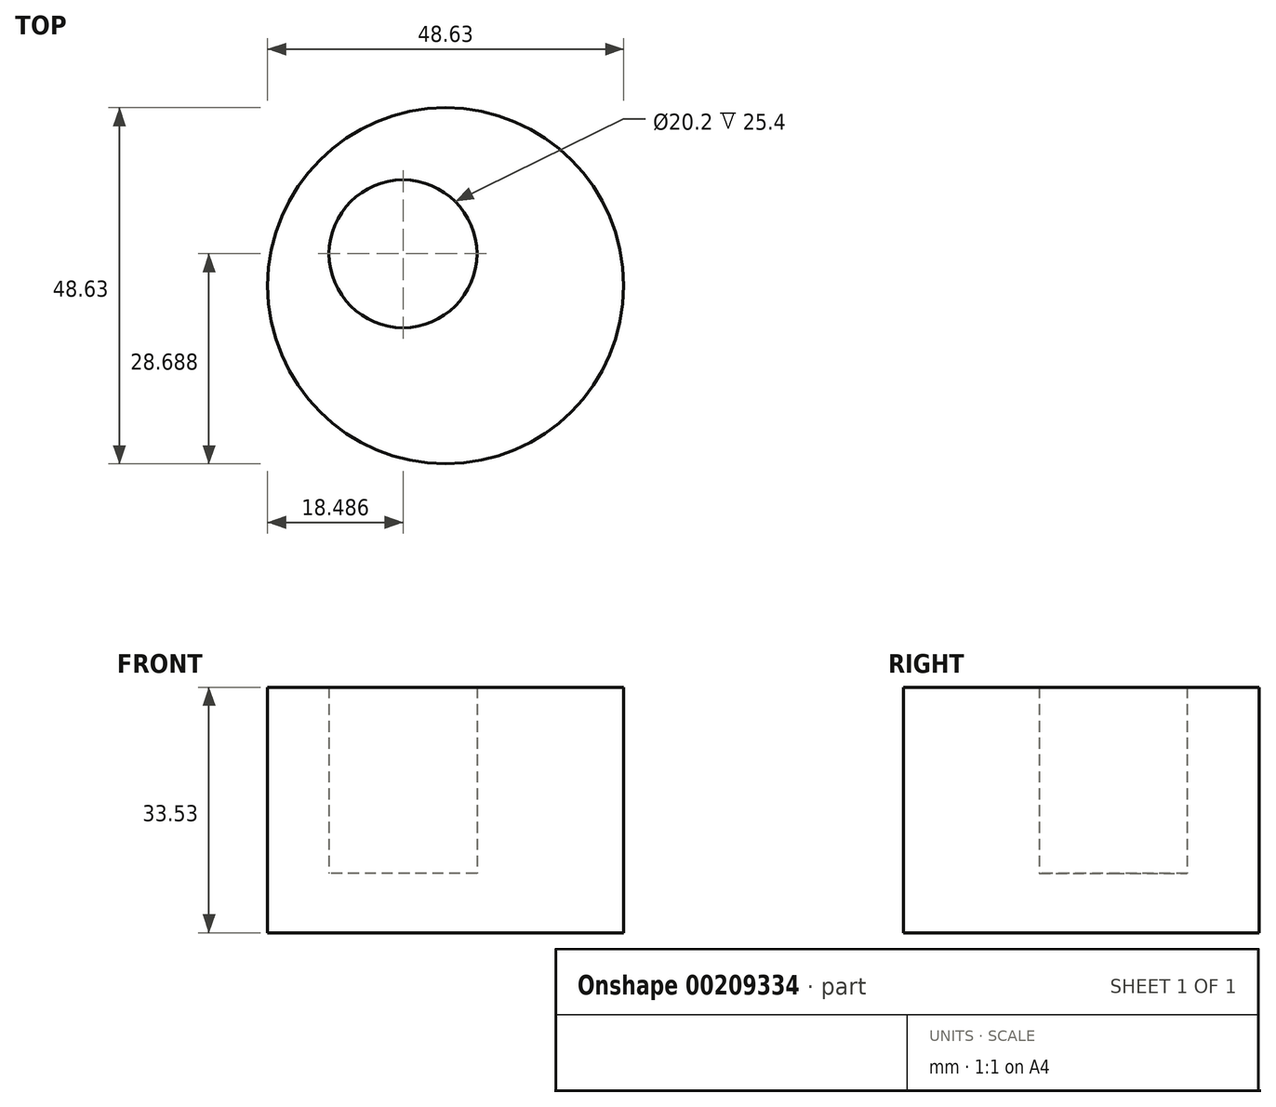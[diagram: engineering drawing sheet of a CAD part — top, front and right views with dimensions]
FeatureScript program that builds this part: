
annotation { "Feature Type Name" : "Feature", "Feature Type Description" : "" }
export const myFeature = defineFeature(function(context is Context, id is Id, definition is map)
    precondition{}
    {
        {
            var Q0;
            Q0=qCreatedBy(makeId("Top.planeOp"),FACE);
            var sketch = newSketch(context, id + "F0", { "sketchPlane" : qUnion([Q0])});
            skCircle(sketch, "E0", {"center": v(-18.65, 15.89) * mm, "radius": 24.31 * mm});
            skCircle(sketch, "E1", {"center": v(-18.65, 15.89) * mm, "radius": 30.09 * mm});
            skSolve(sketch);
        }
        {
            var Q0;
            Q0=makeQuery(id+"F0.imprint","IMPRINT",FACE,{"disambiguationData":[TD([[makeQuery(id+"F0.imprint","IMPRINT",EDGE,{"derivedFrom":sQuery(id+"F0.wireOp",EDGE,"E0")}),1.0]])]});
            extrude(context, id + "F1", {"entities" : qUnion([Q0]), "oppositeDirection" : true, "depth" : 33.53 * mm});
        }
        {
            var Q0;
            Q0=makeQuery(id+"F1.opExtrude","CAP_FACE",FACE,{"disambiguationData":[OSD([sQuery(id+"F0.wireOp",EDGE,"E0")])],"isStart":true});
            var sketch = newSketch(context, id + "F2", { "sketchPlane" : qUnion([Q0])});
            skCircle(sketch, "E2", {"center": v(-23.9, 19.97) * mm, "radius": 6.6 * mm});
            skSolve(sketch);
        }
        {
            var Q0;
            Q0=makeQuery(id+"F2.imprint","IMPRINT",FACE,{"disambiguationData":[TD([[makeQuery(id+"F2.imprint","IMPRINT",EDGE,{"derivedFrom":sQuery(id+"F2.wireOp",EDGE,"E2")}),-1.0]])]});
            var Q1;
            Q1=makeQuery(id+"F2.imprint","IMPRINT",FACE,{"disambiguationData":[TD([[makeQuery(id+"F2.imprint","IMPRINT",EDGE,{"derivedFrom":sQuery(id+"F2.wireOp",EDGE,"E2")}),1.0]])]});
            var Q2;
            Q2=makeQuery(id+"F1.opExtrude","CAP_FACE",FACE,{"disambiguationData":[OSD([sQuery(id+"F0.wireOp",EDGE,"E0")])],"isStart":true});
            var Q3;
            Q3=makeQuery(id+"F1.opExtrude","CAP_FACE",FACE,{"disambiguationData":[OSD([sQuery(id+"F0.wireOp",EDGE,"E0")])],"isStart":false});
            var Q4;
            Q4=sQuery(id+"F2.wireOp",EDGE,"E2");
            extrude(context, id + "F3", {"entities" : qUnion([Q0, Q1, Q2, Q3]), "operationType" : NewBodyOperationType.REMOVE, "surfaceEntities" : qUnion([Q4]), "oppositeDirection" : true, "depth" : 25.4 * mm});
        }
        {
            var Q0;
            {var subQ0=sQuery(id+"F0.wireOp",EDGE,"E0");Q0=makeQuery(id+"F3.boolean.opBoolean","COPY",FACE,{"derivedFrom":makeQuery(id+"F3.opExtrude","CAP_FACE",FACE,{"disambiguationData":[OSD([subQ0]),TDD([makeQuery(id+"F2.imprint","IMPRINT",EDGE,{"derivedFrom":makeQuery(id+"F1.opExtrude","CAP_EDGE",EDGE,{"disambiguationData":[OSD([subQ0])],"isStart":true})})])],"isStart":false})});}
            var sketch = newSketch(context, id + "F4", { "sketchPlane" : qUnion([Q0])});
            skCircle(sketch, "E3", {"center": v(-24.48, 20.26) * mm, "radius": 10.1 * mm});
            skSolve(sketch);
        }
        {
            var Q0;
            Q0=makeQuery(id+"F4.imprint","IMPRINT",FACE,{"disambiguationData":[TD([[makeQuery(id+"F4.imprint","IMPRINT",EDGE,{"derivedFrom":sQuery(id+"F4.wireOp",EDGE,"E3")}),-1.0]])]});
            extrude(context, id + "F5", {"entities" : qUnion([Q0]), "operationType" : NewBodyOperationType.ADD, "depth" : 25.4 * mm});
        }
    });
